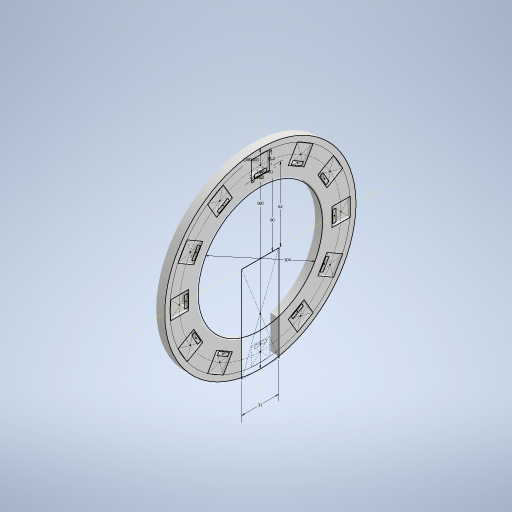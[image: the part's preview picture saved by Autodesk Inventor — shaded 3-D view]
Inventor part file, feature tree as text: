
AUTODESK INVENTOR PART (.ipt)
format: ipt  version: 2024.2 (Build 282272000, 272)  size: 416,768 bytes
history: native  units: mm
features: extrude x2, other x1, sketch x1
ambient origin geometry x8: Origin, YZ Plane, XZ Plane, XY Plane, X Axis, Y Axis, Z Axis, Center Point
bodies: Body1 (feature_tree)
feature tree (4):
  other  "Bryła1"
  sketch  "Szkic1"
  extrude  "Wyciągnięcie proste1"  Depth=15.2mm
  extrude  "Wyciągnięcie proste2"  Depth=15.2mm
